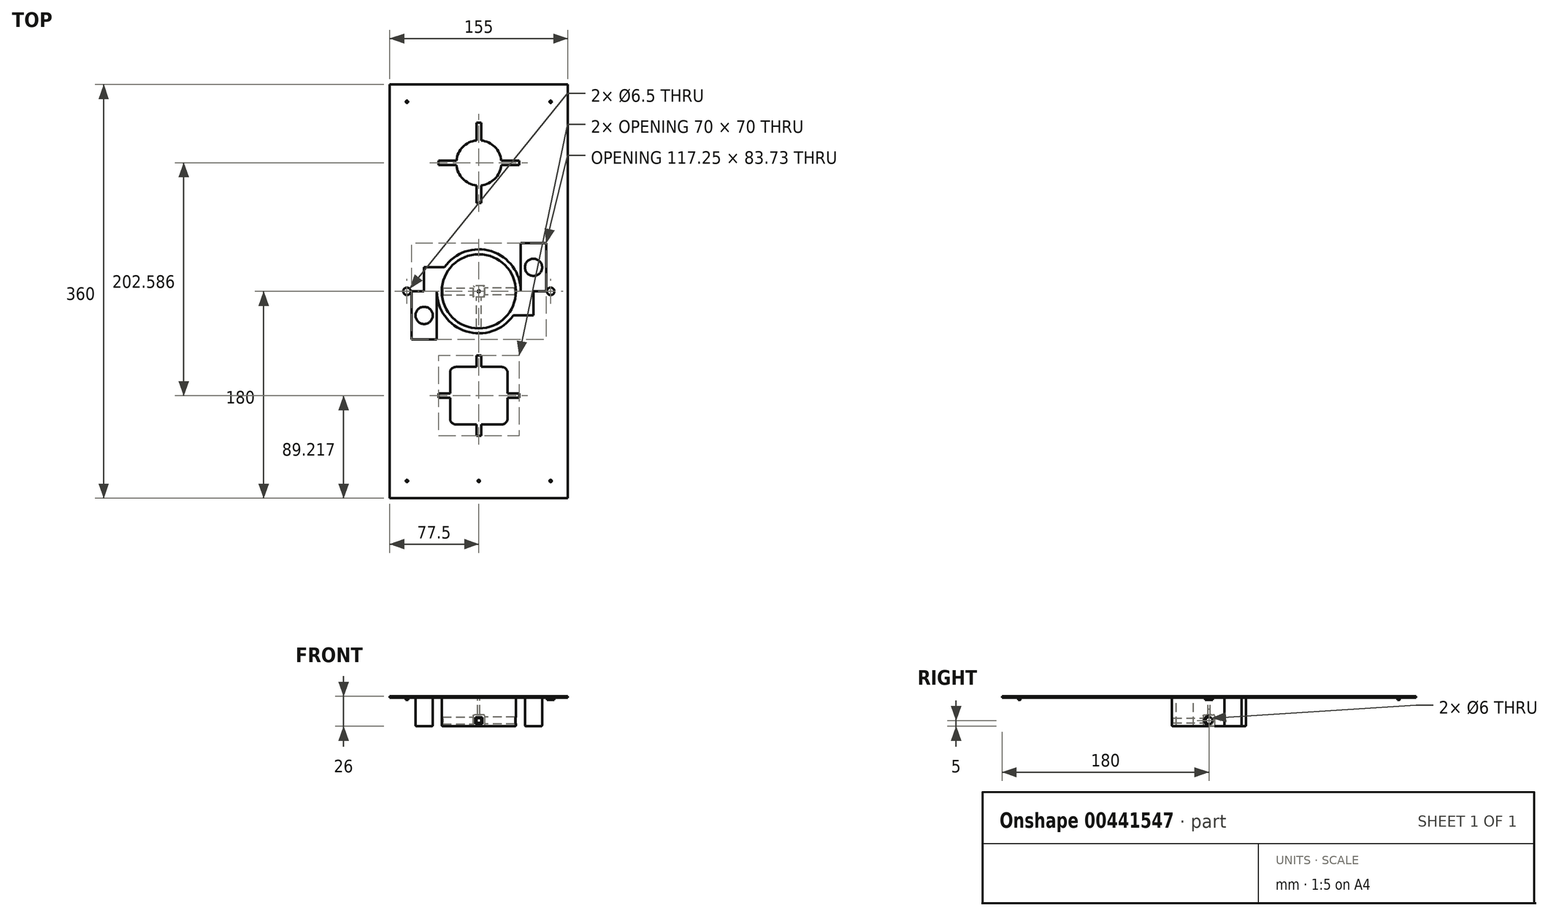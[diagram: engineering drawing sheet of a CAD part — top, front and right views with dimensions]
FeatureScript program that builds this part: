
annotation { "Feature Type Name" : "Feature", "Feature Type Description" : "" }
export const myFeature = defineFeature(function(context is Context, id is Id, definition is map)
    precondition{}
    {
        {
            var Q0;
            Q0=qCreatedBy(makeId("Top.planeOp"),FACE);
            var sketch = newSketch(context, id + "F0", { "sketchPlane" : qUnion([Q0])});
            skLineSegment(sketch, "E0.bottom", {"start": v(77.5, -180) * mm, "end": v(-77.5, -180) * mm});
            skLineSegment(sketch, "E0.top", {"start": v(77.5, 180) * mm, "end": v(-77.5, 180) * mm});
            skLineSegment(sketch, "E0.left", {"start": v(77.5, -180) * mm, "end": v(77.5, 180) * mm});
            skLineSegment(sketch, "E0.right", {"start": v(-77.5, -180) * mm, "end": v(-77.5, 180) * mm});
            skPoint(sketch, "E0.middle", {"position": v(0, 0) * mm});
            skSolve(sketch);
        }
        {
            var Q0;
            Q0=makeQuery(id+"F0.imprint","IMPRINT",FACE,{"disambiguationData":[TD([[makeQuery(id+"F0.imprint","IMPRINT",EDGE,{"derivedFrom":sQuery(id+"F0.wireOp",EDGE,"E0.bottom")}),-1.0]])]});
            extrude(context, id + "F1", {"entities" : qUnion([Q0]), "depth" : 2 * mm});
        }
        {
            var Q0;
            Q0=makeQuery(id+"F1.opExtrude","CAP_FACE",FACE,{"disambiguationData":[OSD([sQuery(id+"F0.wireOp",EDGE,"E0.bottom"),sQuery(id+"F0.wireOp",EDGE,"E0.top"),sQuery(id+"F0.wireOp",EDGE,"E0.left"),sQuery(id+"F0.wireOp",EDGE,"E0.right")])],"isStart":false});
            var sketch = newSketch(context, id + "F2", { "sketchPlane" : qUnion([Q0])});
            skCircle(sketch, "E1", {"center": v(-62.5, 165) * mm, "radius": 1 * mm});
            skCircle(sketch, "E2.MirrorC", {"center": v(62.5, 165) * mm, "radius": 1 * mm});
            skCircle(sketch, "E3.MirrorC", {"center": v(-62.5, -165) * mm, "radius": 1 * mm});
            skCircle(sketch, "E4.MirrorC", {"center": v(62.5, -165) * mm, "radius": 1 * mm});
            skCircle(sketch, "E5", {"center": v(-62.5, 0) * mm, "radius": 3.25 * mm});
            skCircle(sketch, "E6.MirrorC", {"center": v(62.5, 0) * mm, "radius": 3.25 * mm});
            skCircle(sketch, "E7", {"center": v(0, 0) * mm, "radius": 1 * mm});
            skSolve(sketch);
        }
        {
            var Q0;
            Q0=makeQuery(id+"F2.imprint","IMPRINT",FACE,{"disambiguationData":[TD([[makeQuery(id+"F2.imprint","IMPRINT",EDGE,{"derivedFrom":sQuery(id+"F2.wireOp",EDGE,"E1")}),1.0]])]});
            var Q1;
            Q1=makeQuery(id+"F2.imprint","IMPRINT",FACE,{"disambiguationData":[TD([[makeQuery(id+"F2.imprint","IMPRINT",EDGE,{"derivedFrom":sQuery(id+"F2.wireOp",EDGE,"E2.MirrorC")}),-1.0]])]});
            var Q2;
            Q2=makeQuery(id+"F2.imprint","IMPRINT",FACE,{"disambiguationData":[TD([[makeQuery(id+"F2.imprint","IMPRINT",EDGE,{"derivedFrom":sQuery(id+"F2.wireOp",EDGE,"E3.MirrorC")}),-1.0]])]});
            var Q3;
            Q3=makeQuery(id+"F2.imprint","IMPRINT",FACE,{"disambiguationData":[TD([[makeQuery(id+"F2.imprint","IMPRINT",EDGE,{"derivedFrom":sQuery(id+"F2.wireOp",EDGE,"E4.MirrorC")}),1.0]])]});
            var Q4;
            Q4=makeQuery(id+"F2.imprint","IMPRINT",FACE,{"disambiguationData":[TD([[makeQuery(id+"F2.imprint","IMPRINT",EDGE,{"derivedFrom":sQuery(id+"F2.wireOp",EDGE,"E5")}),1.0]])]});
            var Q5;
            Q5=makeQuery(id+"F2.imprint","IMPRINT",FACE,{"disambiguationData":[TD([[makeQuery(id+"F2.imprint","IMPRINT",EDGE,{"derivedFrom":sQuery(id+"F2.wireOp",EDGE,"E6.MirrorC")}),-1.0]])]});
            var Q6;
            Q6=makeQuery(id+"F2.imprint","IMPRINT",FACE,{"disambiguationData":[TD([[makeQuery(id+"F2.imprint","IMPRINT",EDGE,{"derivedFrom":sQuery(id+"F2.wireOp",EDGE,"E7")}),1.0]])]});
            extrude(context, id + "F3", {"entities" : qUnion([Q0, Q1, Q2, Q3, Q4, Q5, Q6]), "operationType" : NewBodyOperationType.REMOVE, "oppositeDirection" : true, "depth" : 25 * mm});
        }
        {
            var Q0;
            Q0=makeQuery(id+"F2.imprint","IMPRINT",FACE,{"disambiguationData":[TD([[makeQuery(id+"F2.imprint","IMPRINT",EDGE,{"derivedFrom":sQuery(id+"F2.wireOp",EDGE,"E1")}),-1.0]])]});
            var sketch = newSketch(context, id + "F4", { "sketchPlane" : qUnion([Q0])});
            skArc(sketch, "E8", {"start": v(36.54, 0) * mm, "mid": v(10.97, 34.85) * mm, "end": v(-29.94, 20.93) * mm});
            skLineSegment(sketch, "E9.top", {"start": v(47.58, -20.93) * mm, "end": v(29.94, -20.93) * mm});
            skLineSegment(sketch, "E9.left", {"start": v(47.58, 0) * mm, "end": v(47.58, -20.93) * mm});
            skLineSegment(sketch, "E9.right", {"start": v(-47.58, 20.93) * mm, "end": v(-47.58, 0) * mm});
            skLineSegment(sketch, "E10.bottom", {"start": v(47.58, 0) * mm, "end": v(58.63, 0) * mm});
            skLineSegment(sketch, "E10.top", {"start": v(36.54, 41.87) * mm, "end": v(58.63, 41.87) * mm});
            skLineSegment(sketch, "E10.left", {"start": v(36.54, 0) * mm, "end": v(36.54, 41.87) * mm});
            skLineSegment(sketch, "E10.right", {"start": v(58.63, 0) * mm, "end": v(58.63, 41.87) * mm});
            skPoint(sketch, "E10.middle", {"position": v(47.58, 20.93) * mm});
            skLineSegment(sketch, "E11.bottom", {"start": v(-47.58, 0) * mm, "end": v(-58.63, 0) * mm});
            skLineSegment(sketch, "E11.top", {"start": v(-36.54, -41.87) * mm, "end": v(-58.63, -41.87) * mm});
            skLineSegment(sketch, "E11.left", {"start": v(-36.54, 0) * mm, "end": v(-36.54, -41.87) * mm});
            skLineSegment(sketch, "E11.right", {"start": v(-58.63, 0) * mm, "end": v(-58.63, -41.87) * mm});
            skPoint(sketch, "E11.middle", {"position": v(-47.58, -20.93) * mm});
            skLineSegment(sketch, "E12.trimOffspring", {"start": v(-29.94, 20.93) * mm, "end": v(-47.58, 20.93) * mm});
            skArc(sketch, "E13.trimOffspring", {"start": v(-36.54, 0) * mm, "mid": v(-10.97, -34.85) * mm, "end": v(29.94, -20.93) * mm});
            skCircle(sketch, "E14", {"center": v(0, 0) * mm, "radius": 32.28 * mm});
            skCircle(sketch, "E15", {"center": v(-47.58, -20.93) * mm, "radius": 7.5 * mm});
            skCircle(sketch, "E16", {"center": v(47.58, 20.93) * mm, "radius": 7.5 * mm});
            skSolve(sketch);
        }
        {
            var Q0;
            {var subQ5=sQuery(id+"F4.wireOp",EDGE,"E10.top");Q0=makeQuery(id+"F4.imprint","IMPRINT",FACE,{"disambiguationData":[TD([[makeQuery(id+"F4.imprint","IMPRINT",EDGE,{"derivedFrom":subQ5}),1.0]])]});}
            extrude(context, id + "F5", {"entities" : qUnion([Q0]), "operationType" : NewBodyOperationType.ADD, "depth" : 1 * mm});
        }
        {
            var Q0;
            Q0=makeQuery(id+"F4.imprint","IMPRINT",FACE,{"disambiguationData":[TD([[makeQuery(id+"F4.imprint","IMPRINT",EDGE,{"derivedFrom":sQuery(id+"F4.wireOp",EDGE,"E14")}),1.0]])]});
            var Q1;
            Q1=makeQuery(id+"F4.imprint","IMPRINT",FACE,{"disambiguationData":[TD([[makeQuery(id+"F4.imprint","IMPRINT",EDGE,{"derivedFrom":sQuery(id+"F4.wireOp",EDGE,"E15")}),1.0]])]});
            var Q2;
            Q2=makeQuery(id+"F4.imprint","IMPRINT",FACE,{"disambiguationData":[TD([[makeQuery(id+"F4.imprint","IMPRINT",EDGE,{"derivedFrom":sQuery(id+"F4.wireOp",EDGE,"E16")}),1.0]])]});
            extrude(context, id + "F6", {"entities" : qUnion([Q0, Q1, Q2]), "operationType" : NewBodyOperationType.ADD, "oppositeDirection" : true, "depth" : 25 * mm});
        }
        {
            var Q0;
            Q0=makeQuery(id+"F6.opExtrude","CAP_EDGE",EDGE,{"disambiguationData":[OSD([sQuery(id+"F4.wireOp",EDGE,"E16")])],"isStart":false});
            var Q1;
            Q1=makeQuery(id+"F6.opExtrude","CAP_EDGE",EDGE,{"disambiguationData":[OSD([sQuery(id+"F4.wireOp",EDGE,"E15")])],"isStart":false});
            var Q2;
            Q2=makeQuery(id+"F6.opExtrude","CAP_EDGE",EDGE,{"disambiguationData":[OSD([sQuery(id+"F4.wireOp",EDGE,"E14")])],"isStart":false});
            fillet(context, id + "F7", {"entities" : qUnion([Q0, Q1, Q2]), "radius" : 1 * mm, "tangentPropagation" : true, "allowEdgeOverflow" : false});
        }
        {
            var Q0;
            Q0=makeQuery(id+"F6.opExtrude","CAP_FACE",FACE,{"disambiguationData":[OSD([sQuery(id+"F2.wireOp",EDGE,"E7"),sQuery(id+"F4.wireOp",EDGE,"E14")])],"isStart":false});
            var sketch = newSketch(context, id + "F8", { "sketchPlane" : qUnion([Q0])});
            skLineSegment(sketch, "E17.bottom", {"start": v(5, 5) * mm, "end": v(-5, 5) * mm});
            skLineSegment(sketch, "E17.top", {"start": v(5, -5) * mm, "end": v(-5, -5) * mm});
            skLineSegment(sketch, "E17.left", {"start": v(5, 5) * mm, "end": v(5, -5) * mm});
            skLineSegment(sketch, "E17.right", {"start": v(-5, 5) * mm, "end": v(-5, -5) * mm});
            skPoint(sketch, "E17.middle", {"position": v(0, 0) * mm});
            skSolve(sketch);
        }
        {
            var Q0;
            Q0=makeQuery(id+"F8.imprint","IMPRINT",FACE,{"disambiguationData":[TD([[makeQuery(id+"F8.imprint","IMPRINT",EDGE,{"derivedFrom":sQuery(id+"F8.wireOp",EDGE,"E17.bottom")}),1.0]])]});
            extrude(context, id + "F9", {"entities" : qUnion([Q0]), "operationType" : NewBodyOperationType.REMOVE, "oppositeDirection" : true, "depth" : 10 * mm});
        }
        {
            var Q0;
            Q0=makeQuery(id+"F9.boolean.opBoolean","COPY",EDGE,{"derivedFrom":makeQuery(id+"F9.opExtrude","CAP_EDGE",EDGE,{"disambiguationData":[OSD([sQuery(id+"F8.wireOp",EDGE,"E17.right")])],"isStart":false})});
            var Q1;
            Q1=makeQuery(id+"F9.boolean.opBoolean","COPY",EDGE,{"derivedFrom":makeQuery(id+"F9.opExtrude","CAP_EDGE",EDGE,{"disambiguationData":[OSD([sQuery(id+"F8.wireOp",EDGE,"E17.top")])],"isStart":false})});
            var Q2;
            Q2=makeQuery(id+"F9.boolean.opBoolean","COPY",EDGE,{"derivedFrom":makeQuery(id+"F9.opExtrude","CAP_EDGE",EDGE,{"disambiguationData":[OSD([sQuery(id+"F8.wireOp",EDGE,"E17.left")])],"isStart":false})});
            var Q3;
            Q3=makeQuery(id+"F9.boolean.opBoolean","COPY",FACE,{"derivedFrom":makeQuery(id+"F9.opExtrude","CAP_FACE",FACE,{"disambiguationData":[OSD([sQuery(id+"F2.wireOp",EDGE,"E7"),sQuery(id+"F8.wireOp",EDGE,"E17.bottom"),sQuery(id+"F8.wireOp",EDGE,"E17.top"),sQuery(id+"F8.wireOp",EDGE,"E17.left"),sQuery(id+"F8.wireOp",EDGE,"E17.right")])],"isStart":false})});
            var Q4;
            Q4=makeQuery(id+"F9.boolean.opBoolean","COPY",EDGE,{"derivedFrom":makeQuery(id+"F9.opExtrude","CAP_EDGE",EDGE,{"disambiguationData":[OSD([sQuery(id+"F8.wireOp",EDGE,"E17.left")])],"isStart":true})});
            var Q5;
            Q5=makeQuery(id+"F9.boolean.opBoolean","COPY",EDGE,{"derivedFrom":makeQuery(id+"F9.opExtrude","CAP_EDGE",EDGE,{"disambiguationData":[OSD([sQuery(id+"F8.wireOp",EDGE,"E17.top")])],"isStart":true})});
            var Q6;
            Q6=makeQuery(id+"F9.boolean.opBoolean","COPY",EDGE,{"derivedFrom":makeQuery(id+"F9.opExtrude","CAP_EDGE",EDGE,{"disambiguationData":[OSD([sQuery(id+"F8.wireOp",EDGE,"E17.right")])],"isStart":true})});
            var Q7;
            Q7=makeQuery(id+"F9.boolean.opBoolean","COPY",EDGE,{"derivedFrom":makeQuery(id+"F9.opExtrude","CAP_EDGE",EDGE,{"disambiguationData":[OSD([sQuery(id+"F8.wireOp",EDGE,"E17.bottom")])],"isStart":true})});
            fillet(context, id + "F10", {"entities" : qUnion([Q0, Q1, Q2, Q3, Q4, Q5, Q6, Q7]), "radius" : 1 * mm, "tangentPropagation" : true, "allowEdgeOverflow" : false});
        }
        {
            var Q0;
            Q0=makeQuery(id+"F9.boolean.opBoolean","COPY",FACE,{"derivedFrom":makeQuery(id+"F9.opExtrude","SWEPT_FACE",FACE,{"disambiguationData":[OSD([sQuery(id+"F8.wireOp",EDGE,"E17.right")])]})});
            var sketch = newSketch(context, id + "F11", { "sketchPlane" : qUnion([Q0])});
            skCircle(sketch, "E18", {"center": v(0, -18) * mm, "radius": 3 * mm});
            skSolve(sketch);
        }
        {
            var Q0;
            Q0 = qSketchRegion(id + "F11", true);
            extrude(context, id + "F12", {"entities" : qUnion([Q0]), "operationType" : NewBodyOperationType.REMOVE, "oppositeDirection" : true, "depth" : 40 * mm});
        }
        {
            var Q0;
            Q0=makeQuery(id+"F12.boolean.opBoolean","INTERSECT",EDGE,{"derivedFrom":[makeQuery(id+"F6.opExtrude","SWEPT_FACE",FACE,{"disambiguationData":[OSD([sQuery(id+"F4.wireOp",EDGE,"E14")])]}),makeQuery(id+"F12.opExtrude","SWEPT_FACE",FACE,{"disambiguationData":[OSD([sQuery(id+"F11.wireOp",EDGE,"E18")])]})]});
            fillet(context, id + "F13", {"entities" : qUnion([Q0]), "radius" : 1 * mm, "tangentPropagation" : true, "allowEdgeOverflow" : false});
        }
        {
            var Q0;
            Q0=makeQuery(id+"F0.imprint","IMPRINT",FACE,{"disambiguationData":[TD([[makeQuery(id+"F0.imprint","IMPRINT",EDGE,{"derivedFrom":sQuery(id+"F0.wireOp",EDGE,"E0.bottom")}),-1.0]])]});
            var sketch = newSketch(context, id + "F14", { "sketchPlane" : qUnion([Q0])});
            skLineSegment(sketch, "E19.bottom", {"start": v(20, -65.78) * mm, "end": v(2, -65.78) * mm});
            skLineSegment(sketch, "E19.top", {"start": v(20, -115.78) * mm, "end": v(2, -115.78) * mm});
            skLineSegment(sketch, "E19.left", {"start": v(25, -70.78) * mm, "end": v(25, -88.78) * mm});
            skLineSegment(sketch, "E19.right", {"start": v(-25, -70.78) * mm, "end": v(-25, -88.78) * mm});
            skPoint(sketch, "E19.middle", {"position": v(0, -90.78) * mm});
            skArc(sketch, "E20", {"start": v(-19.54, 109.88) * mm, "mid": v(-13.9, 97.95) * mm, "end": v(-2, 92.27) * mm});
            skPoint(sketch, "E21.visualSharp", {"position": v(-25, -115.78) * mm});
            skArc(sketch, "E21.filletArc", {"start": v(-25, -110.78) * mm, "mid": v(-23.54, -114.32) * mm, "end": v(-20, -115.78) * mm});
            skPoint(sketch, "E22.visualSharp", {"position": v(25, -115.78) * mm});
            skArc(sketch, "E22.filletArc", {"start": v(20, -115.78) * mm, "mid": v(23.54, -114.32) * mm, "end": v(25, -110.78) * mm});
            skPoint(sketch, "E23.visualSharp", {"position": v(25, -65.78) * mm});
            skArc(sketch, "E23.filletArc", {"start": v(25, -70.78) * mm, "mid": v(23.54, -67.25) * mm, "end": v(20, -65.78) * mm});
            skPoint(sketch, "E24.visualSharp", {"position": v(-25, -65.78) * mm});
            skArc(sketch, "E24.filletArc", {"start": v(-20, -65.78) * mm, "mid": v(-23.54, -67.25) * mm, "end": v(-25, -70.78) * mm});
            skLineSegment(sketch, "E25.bottom", {"start": v(35, 109.88) * mm, "end": v(19.54, 109.88) * mm});
            skLineSegment(sketch, "E25.top", {"start": v(35, 113.73) * mm, "end": v(19.54, 113.73) * mm});
            skLineSegment(sketch, "E25.left", {"start": v(35, 109.88) * mm, "end": v(35, 113.73) * mm});
            skLineSegment(sketch, "E25.right", {"start": v(-35, 109.88) * mm, "end": v(-35, 113.73) * mm});
            skArc(sketch, "E26.trimOffspring", {"start": v(19.54, 113.73) * mm, "mid": v(13.9, 125.66) * mm, "end": v(2, 131.33) * mm});
            skLineSegment(sketch, "E27.trimOffspring", {"start": v(-19.54, 109.88) * mm, "end": v(-35, 109.88) * mm});
            skLineSegment(sketch, "E28.trimOffspring", {"start": v(-19.54, 113.73) * mm, "end": v(-35, 113.73) * mm});
            skLineSegment(sketch, "E29.bottom", {"start": v(2, 76.8) * mm, "end": v(-2, 76.8) * mm});
            skLineSegment(sketch, "E29.top", {"start": v(2, 146.8) * mm, "end": v(-2, 146.8) * mm});
            skLineSegment(sketch, "E29.left", {"start": v(2, 76.8) * mm, "end": v(2, 92.27) * mm});
            skLineSegment(sketch, "E29.right", {"start": v(-2, 76.8) * mm, "end": v(-2, 92.27) * mm});
            skLineSegment(sketch, "E30.trimOffspring", {"start": v(2, 131.33) * mm, "end": v(2, 146.8) * mm});
            skLineSegment(sketch, "E31.trimOffspring", {"start": v(-2, 131.33) * mm, "end": v(-2, 146.8) * mm});
            skArc(sketch, "E32.trimOffspring", {"start": v(-2, 131.33) * mm, "mid": v(-13.9, 125.66) * mm, "end": v(-19.54, 113.73) * mm});
            skArc(sketch, "E33.trimOffspring", {"start": v(2, 92.27) * mm, "mid": v(13.9, 97.95) * mm, "end": v(19.54, 109.88) * mm});
            skLineSegment(sketch, "E34.bottom", {"start": v(35, -92.78) * mm, "end": v(25, -92.78) * mm});
            skLineSegment(sketch, "E34.top", {"start": v(35, -88.78) * mm, "end": v(25, -88.78) * mm});
            skLineSegment(sketch, "E34.left", {"start": v(35, -92.78) * mm, "end": v(35, -88.78) * mm});
            skLineSegment(sketch, "E34.right", {"start": v(-35, -92.78) * mm, "end": v(-35, -88.78) * mm});
            skLineSegment(sketch, "E35.bottom", {"start": v(2, -125.78) * mm, "end": v(-2, -125.78) * mm});
            skLineSegment(sketch, "E35.top", {"start": v(2, -55.78) * mm, "end": v(-2, -55.78) * mm});
            skLineSegment(sketch, "E35.left", {"start": v(2, -125.78) * mm, "end": v(2, -115.78) * mm});
            skLineSegment(sketch, "E35.right", {"start": v(-2, -125.78) * mm, "end": v(-2, -115.78) * mm});
            skLineSegment(sketch, "E36.trimOffspring", {"start": v(-2, -115.78) * mm, "end": v(-20, -115.78) * mm});
            skLineSegment(sketch, "E37.trimOffspring", {"start": v(-25, -92.78) * mm, "end": v(-35, -92.78) * mm});
            skLineSegment(sketch, "E38.trimOffspring", {"start": v(-25, -88.78) * mm, "end": v(-35, -88.78) * mm});
            skLineSegment(sketch, "E39.trimOffspring", {"start": v(2, -65.78) * mm, "end": v(2, -55.78) * mm});
            skLineSegment(sketch, "E40.trimOffspring", {"start": v(-2, -65.78) * mm, "end": v(-2, -55.78) * mm});
            skLineSegment(sketch, "E41.trimOffspring", {"start": v(-25, -92.78) * mm, "end": v(-25, -110.78) * mm});
            skLineSegment(sketch, "E42.trimOffspring", {"start": v(-2, -65.78) * mm, "end": v(-20, -65.78) * mm});
            skLineSegment(sketch, "E43.trimOffspring", {"start": v(25, -92.78) * mm, "end": v(25, -110.78) * mm});
            skSolve(sketch);
        }
        {
            var Q0;
            Q0=makeQuery(id+"F14.imprint","IMPRINT",FACE,{"disambiguationData":[TD([[makeQuery(id+"F14.imprint","IMPRINT",EDGE,{"derivedFrom":sQuery(id+"F14.wireOp",EDGE,"E19.bottom")}),1.0]])]});
            var Q1;
            Q1=makeQuery(id+"F14.imprint","IMPRINT",FACE,{"disambiguationData":[TD([[makeQuery(id+"F14.imprint","IMPRINT",EDGE,{"derivedFrom":sQuery(id+"F14.wireOp",EDGE,"E20")}),1.0]])]});
            extrude(context, id + "F15", {"entities" : qUnion([Q0, Q1]), "operationType" : NewBodyOperationType.REMOVE, "depth" : 25 * mm});
        }
        {
            var Q0;
            Q0=makeQuery(id+"F9.boolean.opBoolean","COPY",FACE,{"derivedFrom":makeQuery(id+"F9.opExtrude","SWEPT_FACE",FACE,{"disambiguationData":[OSD([sQuery(id+"F8.wireOp",EDGE,"E17.left")])]})});
            var sketch = newSketch(context, id + "F16", { "sketchPlane" : qUnion([Q0])});
            skCircle(sketch, "E44", {"center": v(0, -18) * mm, "radius": 3 * mm});
            skSolve(sketch);
        }
        {
            var Q0;
            Q0=makeQuery(id+"F16.imprint","IMPRINT",FACE,{"disambiguationData":[TD([[makeQuery(id+"F16.imprint","IMPRINT",EDGE,{"derivedFrom":sQuery(id+"F16.wireOp",EDGE,"E44")}),1.0]])]});
            extrude(context, id + "F17", {"entities" : qUnion([Q0]), "operationType" : NewBodyOperationType.REMOVE, "oppositeDirection" : true, "depth" : 40 * mm});
        }
        {
            var Q0;
            Q0=makeQuery(id+"F9.boolean.opBoolean","COPY",FACE,{"derivedFrom":makeQuery(id+"F9.opExtrude","SWEPT_FACE",FACE,{"disambiguationData":[OSD([sQuery(id+"F8.wireOp",EDGE,"E17.bottom")])]})});
            var sketch = newSketch(context, id + "F18", { "sketchPlane" : qUnion([Q0])});
            skLineSegment(sketch, "E45.bottom", {"start": v(-2, -20) * mm, "end": v(2, -20) * mm});
            skLineSegment(sketch, "E45.top", {"start": v(-2, -16) * mm, "end": v(2, -16) * mm});
            skLineSegment(sketch, "E45.left", {"start": v(-2, -20) * mm, "end": v(-2, -16) * mm});
            skLineSegment(sketch, "E45.right", {"start": v(2, -20) * mm, "end": v(2, -16) * mm});
            skPoint(sketch, "E45.middle", {"position": v(0, -18) * mm});
            skSolve(sketch);
        }
        {
            var Q0;
            Q0=makeQuery(id+"F18.imprint","IMPRINT",FACE,{"disambiguationData":[TD([[makeQuery(id+"F18.imprint","IMPRINT",EDGE,{"derivedFrom":sQuery(id+"F18.wireOp",EDGE,"E45.bottom")}),1.0]])]});
            extrude(context, id + "F19", {"entities" : qUnion([Q0]), "operationType" : NewBodyOperationType.REMOVE, "oppositeDirection" : true, "depth" : 40 * mm});
        }
        {
            var Q0;
            Q0=makeQuery(id+"F17.boolean.opBoolean","INTERSECT",EDGE,{"derivedFrom":[makeQuery(id+"F6.opExtrude","SWEPT_FACE",FACE,{"disambiguationData":[OSD([sQuery(id+"F4.wireOp",EDGE,"E14")])]}),makeQuery(id+"F17.opExtrude","SWEPT_FACE",FACE,{"disambiguationData":[OSD([sQuery(id+"F16.wireOp",EDGE,"E44")])]})]});
            chamfer(context, id + "F20", {"entities" : qUnion([Q0]), "width" : 1 * mm, "tangentPropagation" : true});
        }
        {
            var Q0;
            Q0=makeQuery(id+"F19.boolean.opBoolean","INTERSECT",EDGE,{"derivedFrom":[makeQuery(id+"F6.opExtrude","SWEPT_FACE",FACE,{"disambiguationData":[OSD([sQuery(id+"F4.wireOp",EDGE,"E14")])]}),makeQuery(id+"F19.opExtrude","SWEPT_FACE",FACE,{"disambiguationData":[OSD([sQuery(id+"F18.wireOp",EDGE,"E45.right")])]})]});
            var Q1;
            Q1=makeQuery(id+"F19.boolean.opBoolean","INTERSECT",EDGE,{"derivedFrom":[makeQuery(id+"F6.opExtrude","SWEPT_FACE",FACE,{"disambiguationData":[OSD([sQuery(id+"F4.wireOp",EDGE,"E14")])]}),makeQuery(id+"F19.opExtrude","SWEPT_FACE",FACE,{"disambiguationData":[OSD([sQuery(id+"F18.wireOp",EDGE,"E45.bottom")])]})]});
            var Q2;
            Q2=makeQuery(id+"F19.boolean.opBoolean","INTERSECT",EDGE,{"derivedFrom":[makeQuery(id+"F6.opExtrude","SWEPT_FACE",FACE,{"disambiguationData":[OSD([sQuery(id+"F4.wireOp",EDGE,"E14")])]}),makeQuery(id+"F19.opExtrude","SWEPT_FACE",FACE,{"disambiguationData":[OSD([sQuery(id+"F18.wireOp",EDGE,"E45.left")])]})]});
            var Q3;
            Q3=makeQuery(id+"F19.boolean.opBoolean","INTERSECT",EDGE,{"derivedFrom":[makeQuery(id+"F6.opExtrude","SWEPT_FACE",FACE,{"disambiguationData":[OSD([sQuery(id+"F4.wireOp",EDGE,"E14")])]}),makeQuery(id+"F19.opExtrude","SWEPT_FACE",FACE,{"disambiguationData":[OSD([sQuery(id+"F18.wireOp",EDGE,"E45.top")])]})]});
            var Q4;
            Q4=makeQuery(id+"F19.boolean.opBoolean","COPY",EDGE,{"derivedFrom":makeQuery(id+"F19.opExtrude","CAP_EDGE",EDGE,{"disambiguationData":[OSD([sQuery(id+"F18.wireOp",EDGE,"E45.bottom")])],"isStart":true})});
            var Q5;
            Q5=makeQuery(id+"F19.boolean.opBoolean","COPY",EDGE,{"derivedFrom":makeQuery(id+"F19.opExtrude","CAP_EDGE",EDGE,{"disambiguationData":[OSD([sQuery(id+"F18.wireOp",EDGE,"E45.left")])],"isStart":true})});
            var Q6;
            Q6=makeQuery(id+"F19.boolean.opBoolean","COPY",EDGE,{"derivedFrom":makeQuery(id+"F19.opExtrude","CAP_EDGE",EDGE,{"disambiguationData":[OSD([sQuery(id+"F18.wireOp",EDGE,"E45.top")])],"isStart":true})});
            var Q7;
            Q7=makeQuery(id+"F19.boolean.opBoolean","COPY",EDGE,{"derivedFrom":makeQuery(id+"F19.opExtrude","CAP_EDGE",EDGE,{"disambiguationData":[OSD([sQuery(id+"F18.wireOp",EDGE,"E45.right")])],"isStart":true})});
            chamfer(context, id + "F21", {"entities" : qUnion([Q0, Q1, Q2, Q3, Q4, Q5, Q6, Q7]), "chamferType" : ChamferType.OFFSET_ANGLE, "width" : 1 * mm, "oppositeDirection" : false, "angle" : 45 * degree, "tangentPropagation" : true});
        }
        {
            var Q0;
            Q0=makeQuery(id+"F0.imprint","IMPRINT",FACE,{"disambiguationData":[TD([[makeQuery(id+"F0.imprint","IMPRINT",EDGE,{"derivedFrom":sQuery(id+"F0.wireOp",EDGE,"E0.bottom")}),-1.0]])]});
            var sketch = newSketch(context, id + "F22", { "sketchPlane" : qUnion([Q0])});
            skLineSegment(sketch, "E46", {"start": v(-43.2, -165) * mm, "end": v(43.2, -165) * mm});
            skCircle(sketch, "E47", {"center": v(0, -165) * mm, "radius": 1 * mm});
            skSolve(sketch);
        }
        {
            var Q0;
            {var subQ0=sQuery(id+"F22.wireOp",EDGE,"E47");var subQ1=sQuery(id+"F22.wireOp",EDGE,"E46");var subQ2=makeQuery(id+"F22.imprint","INTERSECT",VERTEX,{"disambiguationData":[OD(0.0)],"derivedFrom":[subQ1,subQ0]});Q0=makeQuery(id+"F22.imprint","IMPRINT",FACE,{"disambiguationData":[TD([[makeQuery(id+"F22.imprint","IMPRINT",EDGE,{"disambiguationData":[TD([[subQ2,-1.0]])],"derivedFrom":subQ1}),-1.0]])]});}
            var Q1;
            {var subQ0=sQuery(id+"F22.wireOp",EDGE,"E47");var subQ1=sQuery(id+"F22.wireOp",EDGE,"E46");var subQ2=makeQuery(id+"F22.imprint","INTERSECT",VERTEX,{"disambiguationData":[OD(0.0)],"derivedFrom":[subQ1,subQ0]});Q1=makeQuery(id+"F22.imprint","IMPRINT",FACE,{"disambiguationData":[TD([[makeQuery(id+"F22.imprint","IMPRINT",EDGE,{"disambiguationData":[TD([[subQ2,-1.0]])],"derivedFrom":subQ1}),1.0]])]});}
            extrude(context, id + "F23", {"entities" : qUnion([Q0, Q1]), "operationType" : NewBodyOperationType.REMOVE, "depth" : 25 * mm});
        }
    });
